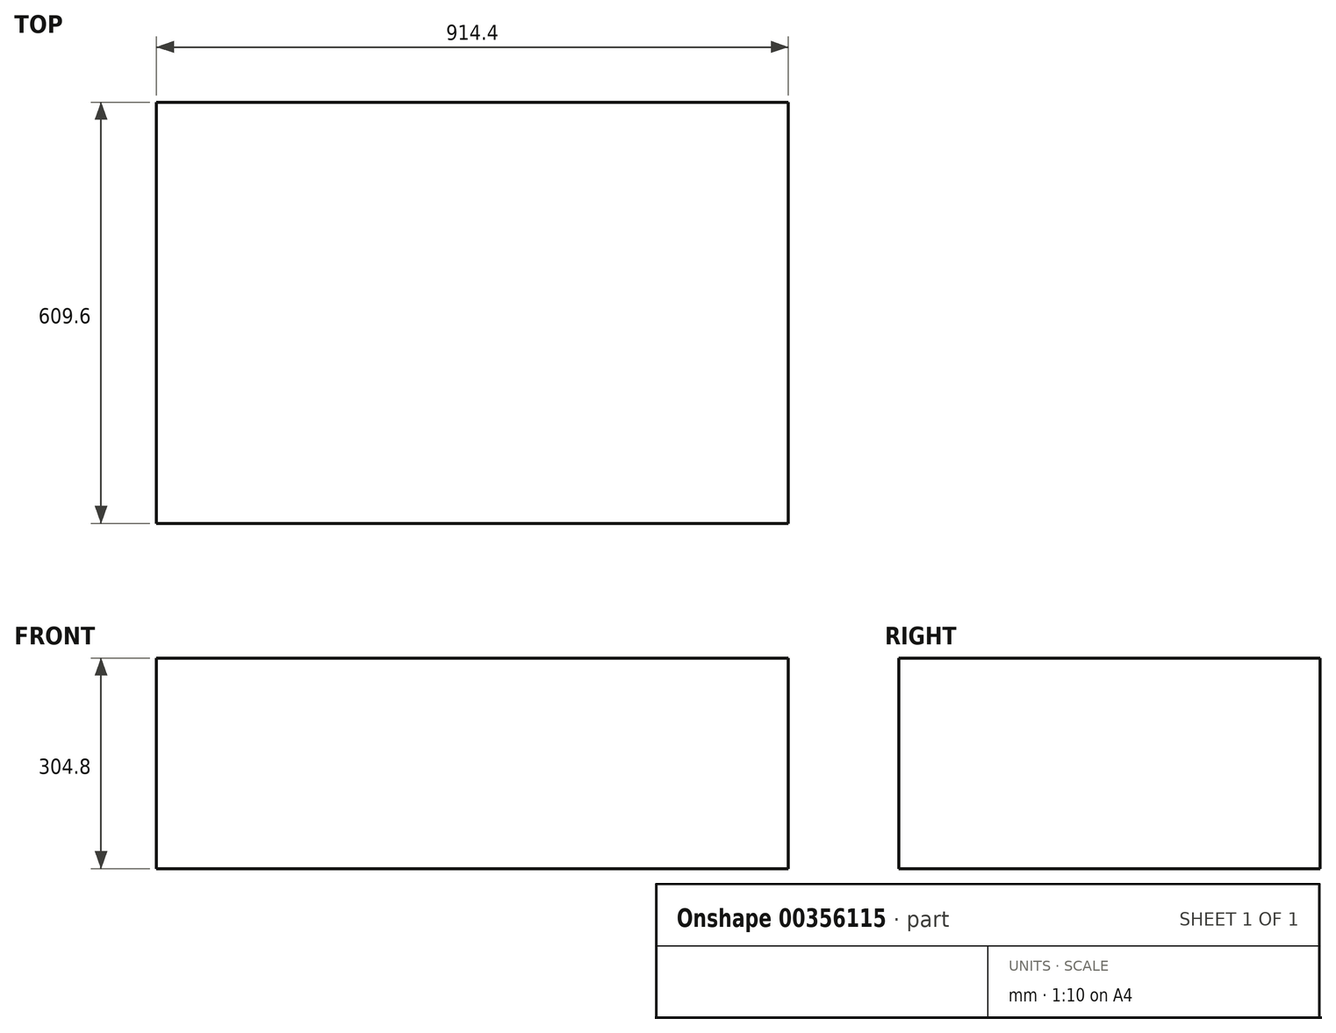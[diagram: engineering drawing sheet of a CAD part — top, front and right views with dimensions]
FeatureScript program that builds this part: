
annotation { "Feature Type Name" : "Feature", "Feature Type Description" : "" }
export const myFeature = defineFeature(function(context is Context, id is Id, definition is map)
    precondition{}
    {
        {
            var Q0;
            Q0=qCreatedBy(makeId("Top.planeOp"),FACE);
            var sketch = newSketch(context, id + "F0", { "sketchPlane" : qUnion([Q0])});
            skLineSegment(sketch, "E0.bottom", {"start": v(-457.2, 304.8) * mm, "end": v(457.2, 304.8) * mm});
            skLineSegment(sketch, "E0.top", {"start": v(-457.2, -304.8) * mm, "end": v(457.2, -304.8) * mm});
            skLineSegment(sketch, "E0.left", {"start": v(-457.2, 304.8) * mm, "end": v(-457.2, -304.8) * mm});
            skLineSegment(sketch, "E0.right", {"start": v(457.2, 304.8) * mm, "end": v(457.2, -304.8) * mm});
            skPoint(sketch, "E0.middle", {"position": v(0, 0) * mm});
            skSolve(sketch);
        }
        {
            var Q0;
            Q0=makeQuery(id+"F0.imprint","IMPRINT",FACE,{"disambiguationData":[TD([[makeQuery(id+"F0.imprint","IMPRINT",EDGE,{"derivedFrom":sQuery(id+"F0.wireOp",EDGE,"E0.bottom")}),-1.0]])]});
            extrude(context, id + "F1", {"entities" : qUnion([Q0]), "depth" : 304.8 * mm, "offsetDistance" : 25.4 * mm});
        }
    });
